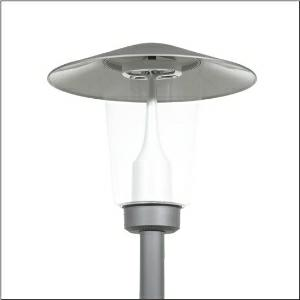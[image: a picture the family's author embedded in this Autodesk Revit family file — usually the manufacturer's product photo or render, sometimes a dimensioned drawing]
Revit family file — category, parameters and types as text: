
# Revit family: pilzleuchte_iq___p1_0a_5xa5235nf14hp_8191
name_source: partatom
category: Lighting Fixtures
units: mm (PartAtom-declared; Revit-internal decimal feet)

## family parameters
Cut with Voids When Loaded = No
Host = Face
Light Source = No
Part Type = Normal
Room Calculation Point = No
Round Connector Dimension = Use Diameter
Shared = No

## types (1)
- --- (1 x LED, 4250 lm, 33.6 W, 2700K)
    Apparent Load = 34 VA
    CIE Flux Codes = 35 64 90 96 100
    Color Rendering = 70
    Color Temperature = 2700K
    Default Elevation = 1800 mm
    Description = Mushroom Luminaire iQ, mast luminaire, Module 540 iQ-SR, primary light control with 3 zone facetted reflector, of plastic, silver coated, highly specular, structured, primary optical cover: cover, of PMMA, transparent, light distribution: P1.0a, light emission: direct distribution, primary light characteristic: strongly asymmetric, installation type: post-top, LED, High Power LED, rated luminous flux: 4.250lm, luminous efficacy: 127lm/W, light colour: 727, colour temperature: 2700K, control gear: iQ Street-Remote, control: pre-setting: logarithmic dimming characteristic, Street-Remote, Auto-Match, Temp-Guard, Lumen-Switch, Night-Set, Smart-Wire, Light-Fading, Desk-Remote (wireless, voltage-free reading and setting of iQ features in the workshop via application-optimized NFC function/RFID function), optimised constant luminous flux control (CLO 2.0), with terminal, 6-pole, max. 2.5mm², mains connection: 230..240V, AC, 50/60Hz, start of lifetime: 34W, end of service life: 36W, reduction: 15W, luminaire housing, upper part, of glass-fibre reinforced polyester, coated, Siteco® metallic grey (DB 702S), diameter: 650mm, height: 586mm, spigot size: d x l = 76 x 70mm (post-top) | with reducer (optional accessory) 60 x 70mm, mounting height: 3..5m, post-top mast mounting element, of diecast aluminium, coated, Siteco® metallic grey (DB 702S), Module 540 iQ-SR, traffic white (RAL 9016), equipment: Power, protection rating (complete): IP65, insulation class (complete): insulation class II (safety insulation), certification: CE, ENEC, VDE, packaging unit: 1 piece

Light Distribution: P1.0a
    Height = 586 mm
    Lamp = 1 x LED
    Lamp Light Flux = 4250 lm
    Lamp Power = 33.6 W
    Lamp count = 1
    Length = 650 mm
    Luminous efficacy = 126 lm/W
    Manufacturer = Siteco
    ModVariant = No
    Model = 5XA5235NF14HP
    Number of Poles = 1
    OnlyDefault = Yes
    Power Factor = 1
    Product Name = Pilzleuchte iQ | P1.0a
    Product group = mast luminaire | pylon top
    ProductGroupID = 6100
    Protection Class = Protection class II
    Protection Degree = IP 65
    RLX_Detail_Level = 1
    RLX_Emergency_Light_Flux = 0 lm
    RLX_Emergency_Type = 0
    RLX_Emergency_Type_DB = No
    RlxData = <blob elided: 52189 chars, md5=4abb522e>
    Socket = socket
    Standby Power = 0 W
    System Light Flux = 4250 lm
    System Power = 34 W
    Type Comments = factory setting: luminous flux: 100 % | dim-lin: 254 | 695 mA
    Type Image = l_1006077.jpg
    URL = http://relux.com
    VarID = @adj_152326
    Voltage = 0 V
    Weight = 0.00 kg
    Width = 0 mm  [stored 0 ft]

note: [stored X ft] marks values corroborated as IEEE doubles in the binary element streams (Revit-internal decimal feet)

## geometry (parser evidence)
native form markers: Blend x4, Sweep x8
no freeform markers — native parametric forms only
